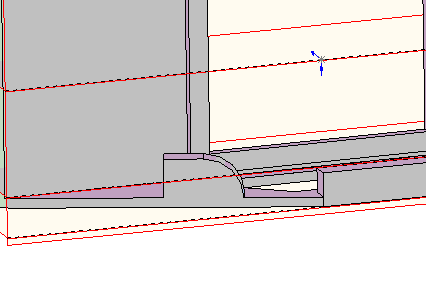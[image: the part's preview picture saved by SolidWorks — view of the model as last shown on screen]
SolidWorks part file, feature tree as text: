
SOLIDWORKS PART (.sldprt)
format: sldprt  version: not decoded by parser v0  size: 376,320 bytes
history: native  units: mm
features: sketch x9, extrude x7, plane x3, cut_extrude x2, fillet x2, mirror x1 (+10 scaffold rows collapsed)
feature tree (34):
  scaffold x10  (default folders/planes/origin — collapsed)
  plane  "Midline"
  plane  "Left edge"  Offset=30.4mm
  plane  "Left mirror edge"  Offset=22mm
  sketch  "Sketch1"  dims[c1.D1=67.88mm c1.D2=33.429mm c1.D3=67.88mm c2.D3=160.0deg c2.D4=25.0mm c2.D5=25.0mm c3.D5=100.0deg c3.D6=25.0mm]
  extrude  "Extrude2"  Depth=2mm
  sketch  "Sketch3"  dims[D1=1.5mm]
  extrude  "Extrude3"  [1 undecoded]
  sketch  "Sketch5"  dims[c1.D1=~23.472852mm c2.D1=~1.335299deg c3.D1=2.0mm c3.D2=~2.004887mm c3.D3=~23.44485mm c4.D1=2.0mm c4.D3=~23.44485mm c5.D3=100.0deg c6.D3=~23.44485mm c7.D3=~0.228426deg c8.D3=~23.44485mm c9.D3=~0.228426deg c10.D3=~23.406929mm c11.D3=~0.03502deg c12.D3=~23.406929mm c13.D3=~0.03502deg c14.D3=2.0mm c14.D4=2.0mm c14.D5=~23.46153mm]
  extrude  "Extrude5"  [1 undecoded]
  sketch  "Sketch8"  dims[D1=20.0mm D2=20.0mm]
  extrude  "Extrude7"  [1 undecoded]
  sketch  "Sketch11"  dims[D1=4.0mm]
  extrude  "Extrude8"  Depth=5mm
  sketch  "Sketch12"  dims[c1.D1=2.5mm c1.D2=25.0mm c1.D3=30.0mm c2.D2=3.0mm c2.D4=2.0mm c2.D5=50.0mm]
  cut_extrude  "Sideport cut"  Depth=4mm
  mirror  "Mirror1"
  sketch  "Sketch9"  dims[c1.D1=25.0mm c1.D2=40.0mm c1.D3=50.0mm c1.D4=7.0mm c2.D2=25.0mm]
  cut_extrude  "Viewport cutout"  Depth=5mm
  sketch  "Sketch10"  dims[c1.D1=4.0mm c1.D2=2.0mm c1.D3=40.0mm c2.D3=~0.615732deg c3.D3=4.0mm c3.D4=4.0mm c3.D5=2.0mm c3.D6=2.0mm c3.D2=4.0mm c4.D4=2.0mm c4.D7=2.0mm c4.D8=4.0mm c4.D9=36.0mm c5.D9=~87.510447deg c5.D7=2.0mm]
  extrude  "Viewport support"  Depth=2mm
  fillet  "Fillet1"  Radius=2mm
  fillet  "Fillet2"  Radius=2mm
  sketch  "Sketch14"  dims[c1.D4=8.0mm c1.D1=36.0mm c1.D2=8.0mm c1.D3=8.0mm c2.D4=~8.164765mm c2.D5=8.0mm]
  extrude  "Extrude9"  Depth=4mm
decode coverage: 17 of 21 modeling features carry decoded parameters
note: ~ marks probable driven/reference dimensions
note: 3 parameter values undecoded
summary: no parameter record found for 3 features
note: suppression state not decoded; provenance and decode notes live in map.json
